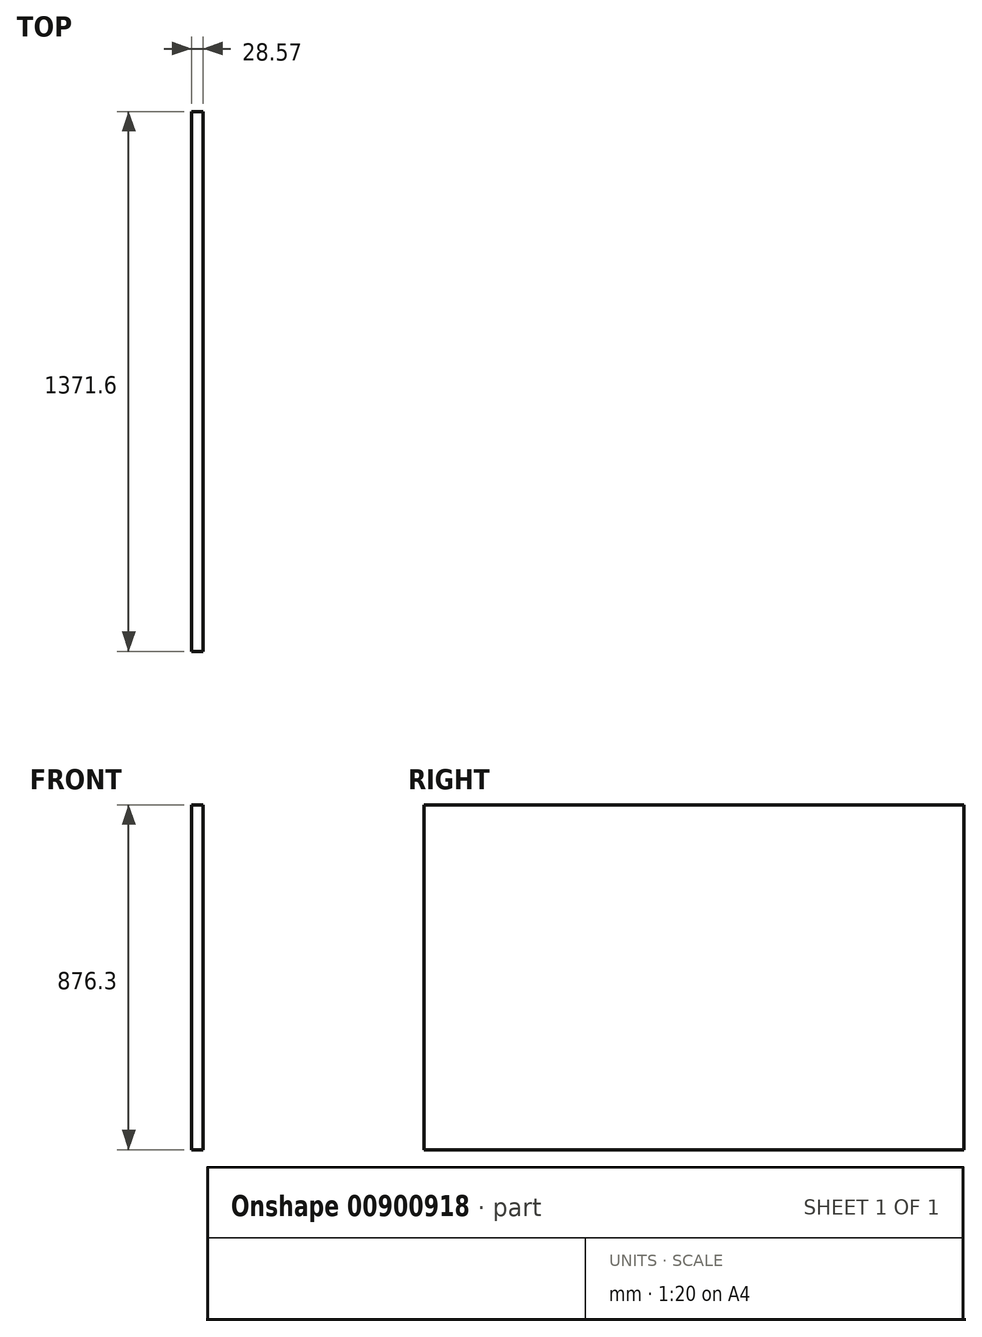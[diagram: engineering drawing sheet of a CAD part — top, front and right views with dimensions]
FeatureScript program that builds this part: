
annotation { "Feature Type Name" : "Feature", "Feature Type Description" : "" }
export const myFeature = defineFeature(function(context is Context, id is Id, definition is map)
    precondition{}
    {
        {
            var Q0;
            Q0=qCreatedBy(makeId("Right.planeOp"),FACE);
            var sketch = newSketch(context, id + "F0", { "sketchPlane" : qUnion([Q0])});
            skLineSegment(sketch, "E0.bottom", {"start": v(685.8, 438.15) * mm, "end": v(-685.8, 438.15) * mm});
            skLineSegment(sketch, "E0.top", {"start": v(685.8, -438.15) * mm, "end": v(-685.8, -438.15) * mm});
            skLineSegment(sketch, "E0.left", {"start": v(685.8, 438.15) * mm, "end": v(685.8, -438.15) * mm});
            skLineSegment(sketch, "E0.right", {"start": v(-685.8, 438.15) * mm, "end": v(-685.8, -438.15) * mm});
            skPoint(sketch, "E0.middle", {"position": v(0, 0) * mm});
            skSolve(sketch);
        }
        {
            var Q0;
            Q0=makeQuery(id+"F0.imprint","IMPRINT",FACE,{"disambiguationData":[TD([[makeQuery(id+"F0.imprint","IMPRINT",EDGE,{"derivedFrom":sQuery(id+"F0.wireOp",EDGE,"E0.bottom")}),1.0]])]});
            extrude(context, id + "F1", {"entities" : qUnion([Q0]), "depth" : 28.57 * mm, "offsetDistance" : 25.4 * mm});
        }
    });
